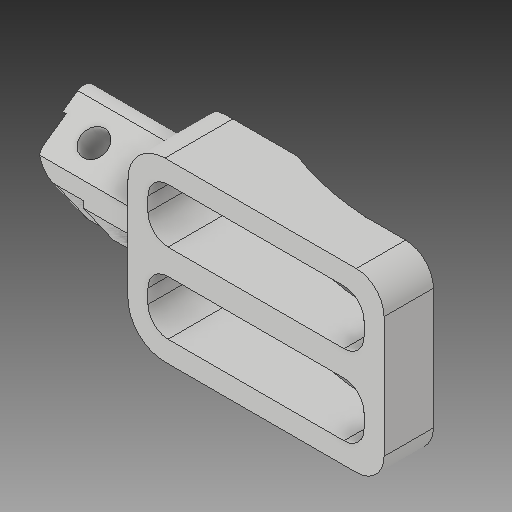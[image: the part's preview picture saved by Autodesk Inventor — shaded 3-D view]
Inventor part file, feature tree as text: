
AUTODESK INVENTOR PART (.ipt)
format: ipt  version: 2019.2 (Build 232265000, 265)  size: 227,328 bytes
history: native  units: mm
features: other x3, mirror x1
ambient origin geometry x8: Origin, YZ Plane, XZ Plane, XY Plane, X Axis, Y Axis, Z Axis, Center Point
bodies: Solid1 (feature_tree)
feature tree (4):
  other  "FootpegLeft.ipt"
  mirror  "Mirror1"
  other  "Solid1::FootpegLeft.ipt"
  other  "TaggingFeature1"
